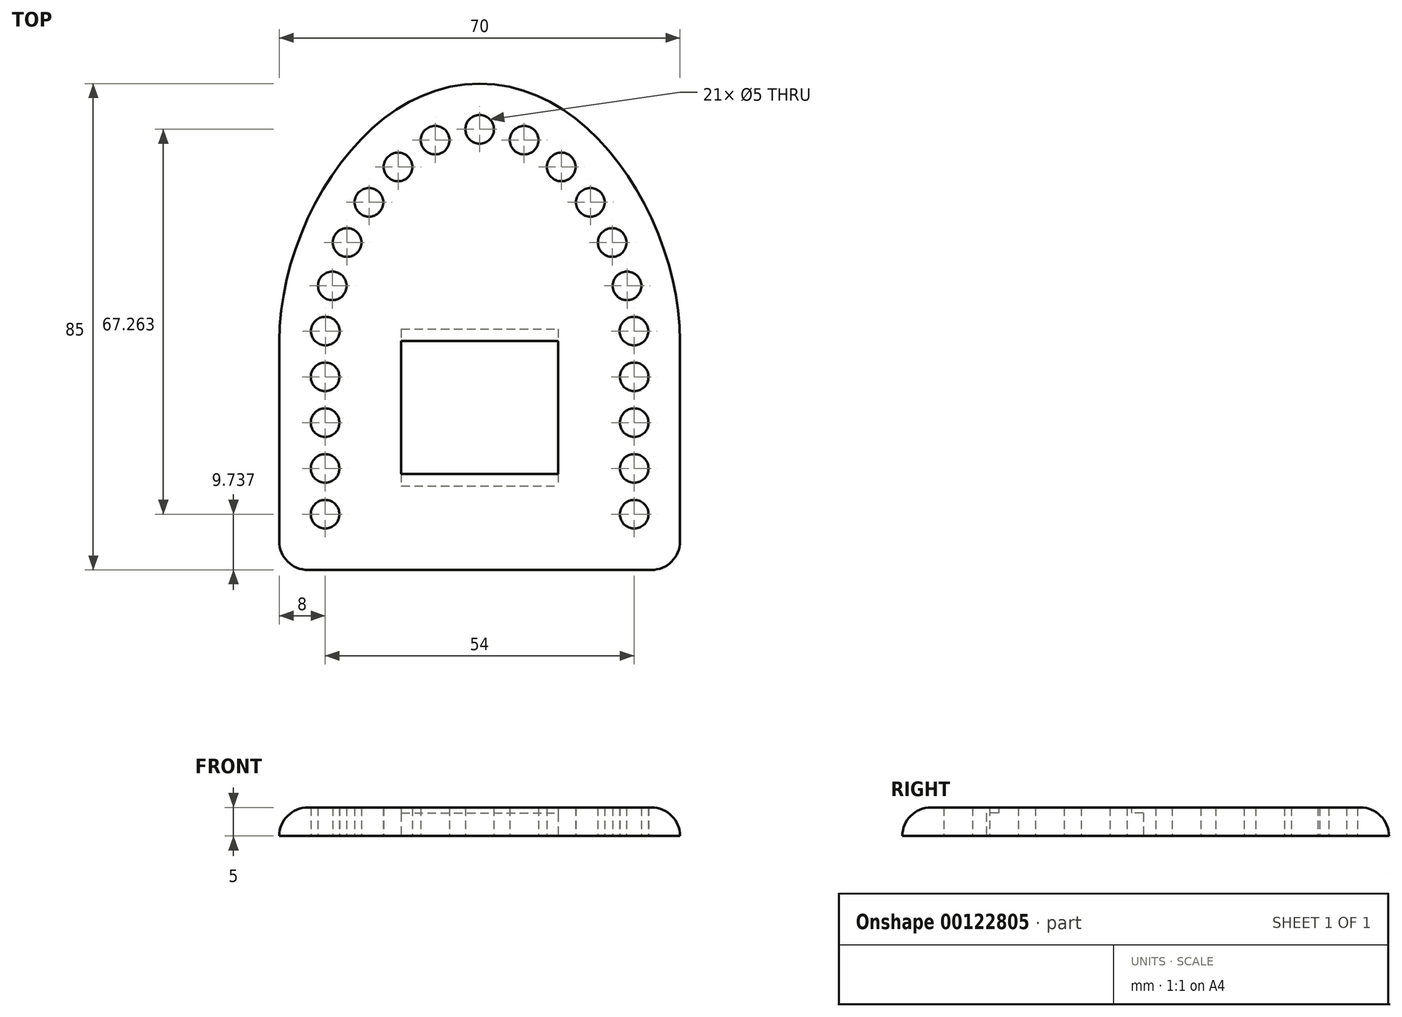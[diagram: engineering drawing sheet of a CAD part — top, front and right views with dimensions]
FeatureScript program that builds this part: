
annotation { "Feature Type Name" : "Feature", "Feature Type Description" : "" }
export const myFeature = defineFeature(function(context is Context, id is Id, definition is map)
    precondition{}
    {
        {
            var Q0;
            Q0=qCreatedBy(makeId("Top.planeOp"),FACE);
            var sketch = newSketch(context, id + "F0", { "sketchPlane" : qUnion([Q0])});
            skLineSegment(sketch, "E0.top", {"start": v(-35, -40) * mm, "end": v(35, -40) * mm});
            skPoint(sketch, "E0.middle", {"position": v(0, 13.14) * mm});
            skPoint(sketch, "E1", {"position": v(0, 0) * mm});
            skCircle(sketch, "E2", {"center": v(0, 0) * mm, "radius": 35 * mm});
            skPoint(sketch, "E3.visualSharp", {"position": v(-35, -40) * mm});
            skPoint(sketch, "E4.visualSharp", {"position": v(35, -40) * mm});
            skPoint(sketch, "E5", {"position": v(-35, 0) * mm});
            skPoint(sketch, "E6", {"position": v(35, 0) * mm});
            skFitSpline(sketch, "E7", {"points": [v(0, 45) * mm, v(-35, 0) * mm], "startDerivative": vector(-60.6, 0) * mm, "endDerivative": vector(0, -60.15) * mm});
            skLineSegment(sketch, "E8", {"start": v(-35, 0) * mm, "end": v(-35, -40) * mm});
            skLineSegment(sketch, "E9", {"start": v(35, 0) * mm, "end": v(35, -40) * mm});
            skFitSpline(sketch, "E10.MirrorCS", {"points": [v(0, 45) * mm, v(35, 0) * mm], "startDerivative": vector(60.6, 0) * mm, "endDerivative": vector(0, -60.15) * mm});
            skFitSpline(sketch, "E11.0", {"points": [v(0, 37) * mm, v(-0.85, 37) * mm, v(-2.51, 36.87) * mm, v(-4.95, 36.3) * mm, v(-7.36, 35.37) * mm, v(-10.54, 33.64) * mm, v(-14.42, 30.55) * mm, v(-18.67, 25.54) * mm, v(-22.24, 19.56) * mm, v(-24.95, 13) * mm, v(-26.62, 6.3) * mm, v(-27, 2.01) * mm, v(-27, 0) * mm]});
            skPoint(sketch, "E12", {"position": v(0, 37) * mm});
            skPoint(sketch, "E13", {"position": v(-7.77, 35.11) * mm});
            skPoint(sketch, "E14", {"position": v(-14.26, 30.43) * mm});
            skPoint(sketch, "E15", {"position": v(-19.34, 24.24) * mm});
            skPoint(sketch, "E16", {"position": v(-23.15, 17.21) * mm});
            skPoint(sketch, "E17", {"position": v(-25.74, 9.64) * mm});
            skLineSegment(sketch, "E18", {"start": v(-27, 0) * mm, "end": v(-27, -40) * mm});
            skPoint(sketch, "E19", {"position": v(-26.96, 1.74) * mm});
            skPoint(sketch, "E20", {"position": v(-27, -6.26) * mm});
            skPoint(sketch, "E21", {"position": v(-27, -14.26) * mm});
            skPoint(sketch, "E22", {"position": v(-27, -22.26) * mm});
            skPoint(sketch, "E23", {"position": v(-27, -30.26) * mm});
            skLineSegment(sketch, "E24.MirrorCS", {"start": v(27, 0) * mm, "end": v(27, -40) * mm});
            skPoint(sketch, "E25.MirrorP", {"position": v(7.77, 35.11) * mm});
            skPoint(sketch, "E26.MirrorP", {"position": v(14.26, 30.43) * mm});
            skPoint(sketch, "E27.MirrorP", {"position": v(19.34, 24.24) * mm});
            skPoint(sketch, "E28.MirrorP", {"position": v(23.15, 17.21) * mm});
            skPoint(sketch, "E29.MirrorP", {"position": v(25.74, 9.64) * mm});
            skPoint(sketch, "E30.MirrorP", {"position": v(26.96, 1.74) * mm});
            skPoint(sketch, "E31.MirrorP", {"position": v(27, -6.26) * mm});
            skPoint(sketch, "E32.MirrorP", {"position": v(27, -14.26) * mm});
            skPoint(sketch, "E33.MirrorP", {"position": v(27, -22.26) * mm});
            skPoint(sketch, "E34.MirrorP", {"position": v(27, -30.26) * mm});
            skFitSpline(sketch, "E35.0", {"points": [v(0, 37) * mm, v(0.85, 37) * mm, v(2.51, 36.87) * mm, v(4.95, 36.3) * mm, v(7.36, 35.37) * mm, v(10.54, 33.64) * mm, v(14.42, 30.55) * mm, v(18.67, 25.54) * mm, v(22.24, 19.56) * mm, v(24.95, 13) * mm, v(26.62, 6.3) * mm, v(27, 2.01) * mm, v(27, 0) * mm]});
            skLineSegment(sketch, "E36.bottom", {"start": v(-13.7, 0) * mm, "end": v(13.7, 0) * mm});
            skLineSegment(sketch, "E36.top", {"start": v(-13.7, -23.2) * mm, "end": v(13.7, -23.2) * mm});
            skLineSegment(sketch, "E36.left", {"start": v(-13.7, 0) * mm, "end": v(-13.7, -23.2) * mm});
            skLineSegment(sketch, "E36.right", {"start": v(13.7, 0) * mm, "end": v(13.7, -23.2) * mm});
            skPoint(sketch, "E36.middle", {"position": v(0, -11.6) * mm});
            skLineSegment(sketch, "E37.bottom", {"start": v(-13.7, 2.1) * mm, "end": v(13.7, 2.1) * mm});
            skLineSegment(sketch, "E37.top", {"start": v(-13.7, -25.3) * mm, "end": v(13.7, -25.3) * mm});
            skLineSegment(sketch, "E37.left", {"start": v(-13.7, 2.1) * mm, "end": v(-13.7, -25.3) * mm});
            skLineSegment(sketch, "E37.right", {"start": v(13.7, 2.1) * mm, "end": v(13.7, -25.3) * mm});
            skSolve(sketch);
        }
        {
            var Q0;
            Q0=qSketchRegion(id+"F0",true);
            var Q1;
            {var subQ0=sQuery(id+"F0.wireOp",EDGE,"E35.0");var subQ1=sQuery(id+"F0.wireOp",EDGE,"E2");var subQ2=makeQuery(id+"F0.imprint","INTERSECT",VERTEX,{"derivedFrom":[subQ1,subQ0]});Q1=makeQuery(id+"F0.imprint","IMPRINT",FACE,{"disambiguationData":[TD([[makeQuery(id+"F0.imprint","IMPRINT",EDGE,{"disambiguationData":[TD([[subQ2,-1.0]])],"derivedFrom":subQ1}),-1.0]])]});}
            var Q2;
            {var subQ3=sQuery(id+"F0.wireOp",EDGE,"E2");var subQ8=sQuery(id+"F0.wireOp",EDGE,"E35.0");var subQ9=makeQuery(id+"F0.imprint","INTERSECT",VERTEX,{"derivedFrom":[subQ3,subQ8]});Q2=makeQuery(id+"F0.imprint","IMPRINT",FACE,{"disambiguationData":[TD([[makeQuery(id+"F0.imprint","IMPRINT",EDGE,{"disambiguationData":[TD([[subQ9,-1.0]])],"derivedFrom":subQ3}),1.0]])]});}
            var Q3;
            {var subQ0=sQuery(id+"F0.wireOp",EDGE,"E36.top");var subQ1=sQuery(id+"F0.wireOp",EDGE,"E2");var subQ2=makeQuery(id+"F0.imprint","INTERSECT",VERTEX,{"disambiguationData":[OD(0.0)],"derivedFrom":[subQ1,subQ0]});Q3=makeQuery(id+"F0.imprint","IMPRINT",FACE,{"disambiguationData":[TD([[makeQuery(id+"F0.imprint","IMPRINT",EDGE,{"disambiguationData":[TD([[subQ2,-1.0]])],"derivedFrom":subQ1}),1.0]])]});}
            var Q4;
            {var subQ0=sQuery(id+"F0.wireOp",EDGE,"E36.bottom");Q4=makeQuery(id+"F0.imprint","IMPRINT",FACE,{"disambiguationData":[TD([[makeQuery(id+"F0.imprint","IMPRINT",EDGE,{"derivedFrom":subQ0}),1.0]])]});}
            var Q5;
            {var subQ0=sQuery(id+"F0.wireOp",EDGE,"E36.top");Q5=makeQuery(id+"F0.imprint","IMPRINT",FACE,{"disambiguationData":[TD([[makeQuery(id+"F0.imprint","IMPRINT",EDGE,{"derivedFrom":subQ0}),-1.0]])]});}
            extrude(context, id + "F1", {"entities" : qUnion([Q0, Q1, Q2, Q3, Q4, Q5]), "depth" : 5 * mm});
        }
        {
            var Q0;
            {var subQ0=sQuery(id+"F0.wireOp",EDGE,"E36.bottom");Q0=makeQuery(id+"F0.imprint","IMPRINT",FACE,{"disambiguationData":[TD([[makeQuery(id+"F0.imprint","IMPRINT",EDGE,{"derivedFrom":subQ0}),1.0]])]});}
            var Q1;
            {var subQ0=sQuery(id+"F0.wireOp",EDGE,"E36.top");Q1=makeQuery(id+"F0.imprint","IMPRINT",FACE,{"disambiguationData":[TD([[makeQuery(id+"F0.imprint","IMPRINT",EDGE,{"derivedFrom":subQ0}),-1.0]])]});}
            extrude(context, id + "F2", {"entities" : qUnion([Q0, Q1]), "operationType" : NewBodyOperationType.REMOVE, "depth" : 4 * mm});
        }
        {
            var Q0;
            Q0=sQuery(id+"F0.wireOp",VERTEX,"E12");
            var Q1;
            Q1=sQuery(id+"F0.wireOp",VERTEX,"E13");
            var Q2;
            Q2=sQuery(id+"F0.wireOp",VERTEX,"E14");
            var Q3;
            Q3=sQuery(id+"F0.wireOp",VERTEX,"E15");
            var Q4;
            Q4=sQuery(id+"F0.wireOp",VERTEX,"E16");
            var Q5;
            Q5=sQuery(id+"F0.wireOp",VERTEX,"E17");
            var Q6;
            Q6=sQuery(id+"F0.wireOp",VERTEX,"E19");
            var Q7;
            Q7=sQuery(id+"F0.wireOp",VERTEX,"E20");
            var Q8;
            Q8=sQuery(id+"F0.wireOp",VERTEX,"E21");
            var Q9;
            Q9=sQuery(id+"F0.wireOp",VERTEX,"E22");
            var Q10;
            Q10=sQuery(id+"F0.wireOp",VERTEX,"E25.MirrorP");
            var Q11;
            Q11=sQuery(id+"F0.wireOp",VERTEX,"E26.MirrorP");
            var Q12;
            Q12=sQuery(id+"F0.wireOp",VERTEX,"E27.MirrorP");
            var Q13;
            Q13=sQuery(id+"F0.wireOp",VERTEX,"E28.MirrorP");
            var Q14;
            Q14=sQuery(id+"F0.wireOp",VERTEX,"E29.MirrorP");
            var Q15;
            Q15=sQuery(id+"F0.wireOp",VERTEX,"E30.MirrorP");
            var Q16;
            Q16=sQuery(id+"F0.wireOp",VERTEX,"E31.MirrorP");
            var Q17;
            Q17=sQuery(id+"F0.wireOp",VERTEX,"E32.MirrorP");
            var Q18;
            Q18=sQuery(id+"F0.wireOp",VERTEX,"E33.MirrorP");
            var Q19;
            Q19=sQuery(id+"F0.wireOp",VERTEX,"E23");
            var Q20;
            Q20=sQuery(id+"F0.wireOp",VERTEX,"E34.MirrorP");
            var Q21;
            Q21=makeQuery(id+"F1.opExtrude","SWEPT_BODY",BODY,{"disambiguationData":[OSD([sQuery(id+"F0.wireOp",EDGE,"E0.top"),sQuery(id+"F0.wireOp",EDGE,"E2"),sQuery(id+"F0.wireOp",EDGE,"E7"),sQuery(id+"F0.wireOp",EDGE,"E8"),sQuery(id+"F0.wireOp",EDGE,"E9"),sQuery(id+"F0.wireOp",EDGE,"E10.MirrorCS"),sQuery(id+"F0.wireOp",EDGE,"E11.0"),sQuery(id+"F0.wireOp",EDGE,"E35.0")])]});
            hole(context, id + "F3", {"style" : HoleStyle.SIMPLE, "endStyle" : HoleEndStyle.THROUGH, "oppositeDirection" : true, "holeDiameter" : 5 * mm, "startFromSketch" : true, "locations" : qUnion([Q0, Q1, Q2, Q3, Q4, Q5, Q6, Q7, Q8, Q9, Q10, Q11, Q12, Q13, Q14, Q15, Q16, Q17, Q18, Q19, Q20]), "scope" : qUnion([Q21]), "isTappedThrough" : true});
        }
        {
            var Q0;
            Q0=makeQuery(id+"F1.opExtrude","SWEPT_EDGE",EDGE,{"disambiguationData":[OSD([sQuery(id+"F0.wireOp",EDGE,"E0.top"),sQuery(id+"F0.wireOp",EDGE,"E8")])]});
            var Q1;
            Q1=makeQuery(id+"F1.opExtrude","SWEPT_EDGE",EDGE,{"disambiguationData":[OSD([sQuery(id+"F0.wireOp",EDGE,"E0.top"),sQuery(id+"F0.wireOp",EDGE,"E9")])]});
            var Q2;
            Q2=makeQuery(id+"F1.opExtrude","CAP_EDGE",EDGE,{"disambiguationData":[OSD([sQuery(id+"F0.wireOp",EDGE,"E8")])],"isStart":false});
            var Q3;
            Q3=makeQuery(id+"F1.opExtrude","CAP_EDGE",EDGE,{"disambiguationData":[OSD([sQuery(id+"F0.wireOp",EDGE,"E0.top")])],"isStart":false});
            fillet(context, id + "F4", {"entities" : qUnion([Q0, Q1, Q2, Q3]), "radius" : 5 * mm, "tangentPropagation" : true, "allowEdgeOverflow" : false});
        }
    });
